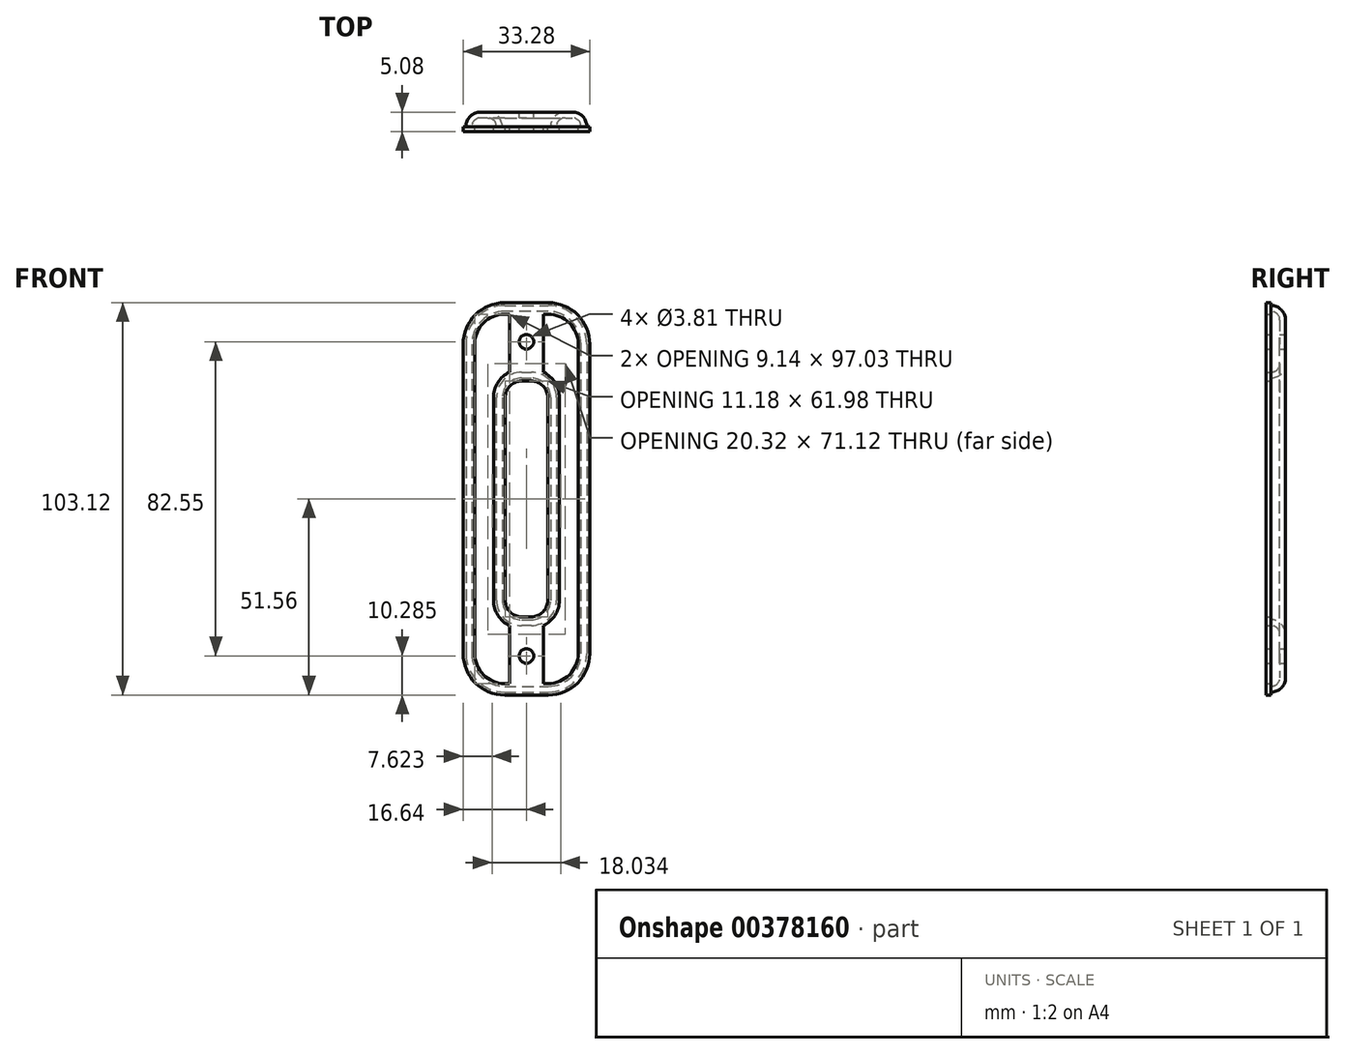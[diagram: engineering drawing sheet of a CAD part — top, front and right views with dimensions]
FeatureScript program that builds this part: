
annotation { "Feature Type Name" : "Feature", "Feature Type Description" : "" }
export const myFeature = defineFeature(function(context is Context, id is Id, definition is map)
    precondition{}
    {
        {
            var Q0;
            Q0=qCreatedBy(makeId("Front.planeOp"),FACE);
            var sketch = newSketch(context, id + "F0", { "sketchPlane" : qUnion([Q0])});
            skLineSegment(sketch, "E0.bottom", {"start": v(-6.35, 31.75) * mm, "end": v(6.35, 31.75) * mm});
            skLineSegment(sketch, "E0.top", {"start": v(-6.35, -31.75) * mm, "end": v(6.35, -31.75) * mm});
            skLineSegment(sketch, "E0.left", {"start": v(-6.35, 31.75) * mm, "end": v(-6.35, -31.75) * mm});
            skLineSegment(sketch, "E0.right", {"start": v(6.35, 31.75) * mm, "end": v(6.35, -31.75) * mm});
            skPoint(sketch, "E0.middle", {"position": v(0, 0) * mm});
            skLineSegment(sketch, "E1.bottom", {"start": v(-15.88, 50.8) * mm, "end": v(15.87, 50.8) * mm});
            skLineSegment(sketch, "E1.top", {"start": v(-15.87, -50.8) * mm, "end": v(15.88, -50.8) * mm});
            skLineSegment(sketch, "E1.left", {"start": v(-15.88, 50.8) * mm, "end": v(-15.87, -50.8) * mm});
            skLineSegment(sketch, "E1.right", {"start": v(15.87, 50.8) * mm, "end": v(15.88, -50.8) * mm});
            skSolve(sketch);
        }
        {
            var Q0;
            Q0 = qSketchRegion(id + "F0", true);
            extrude(context, id + "F1", {"entities" : qUnion([Q0]), "depth" : 3.8 * mm});
        }
        {
            var Q0;
            Q0=makeQuery(id+"F1.opExtrude","SWEPT_EDGE",EDGE,{"disambiguationData":[OSD([sQuery(id+"F0.wireOp",EDGE,"E1.bottom"),sQuery(id+"F0.wireOp",EDGE,"E1.left")])]});
            var Q1;
            Q1=makeQuery(id+"F1.opExtrude","SWEPT_EDGE",EDGE,{"disambiguationData":[OSD([sQuery(id+"F0.wireOp",EDGE,"E1.bottom"),sQuery(id+"F0.wireOp",EDGE,"E1.right")])]});
            var Q2;
            Q2=makeQuery(id+"F1.opExtrude","SWEPT_EDGE",EDGE,{"disambiguationData":[OSD([sQuery(id+"F0.wireOp",EDGE,"E1.top"),sQuery(id+"F0.wireOp",EDGE,"E1.right")])]});
            var Q3;
            Q3=makeQuery(id+"F1.opExtrude","SWEPT_EDGE",EDGE,{"disambiguationData":[OSD([sQuery(id+"F0.wireOp",EDGE,"E1.top"),sQuery(id+"F0.wireOp",EDGE,"E1.left")])]});
            fillet(context, id + "F2", {"entities" : qUnion([Q0, Q1, Q2, Q3]), "radius" : 10.16 * mm, "tangentPropagation" : true, "allowEdgeOverflow" : false});
        }
        {
            var Q0;
            Q0=makeQuery(id+"F1.opExtrude","SWEPT_EDGE",EDGE,{"disambiguationData":[OSD([sQuery(id+"F0.wireOp",EDGE,"E0.bottom"),sQuery(id+"F0.wireOp",EDGE,"E0.left")])]});
            var Q1;
            Q1=makeQuery(id+"F1.opExtrude","SWEPT_EDGE",EDGE,{"disambiguationData":[OSD([sQuery(id+"F0.wireOp",EDGE,"E0.bottom"),sQuery(id+"F0.wireOp",EDGE,"E0.right")])]});
            var Q2;
            Q2=makeQuery(id+"F1.opExtrude","SWEPT_EDGE",EDGE,{"disambiguationData":[OSD([sQuery(id+"F0.wireOp",EDGE,"E0.top"),sQuery(id+"F0.wireOp",EDGE,"E0.left")])]});
            var Q3;
            Q3=makeQuery(id+"F1.opExtrude","SWEPT_EDGE",EDGE,{"disambiguationData":[OSD([sQuery(id+"F0.wireOp",EDGE,"E0.top"),sQuery(id+"F0.wireOp",EDGE,"E0.right")])]});
            fillet(context, id + "F3", {"entities" : qUnion([Q0, Q1, Q2, Q3]), "radius" : 5.08 * mm, "tangentPropagation" : true, "allowEdgeOverflow" : false});
        }
        {
            var Q0;
            Q0=makeQuery(id+"F1.opExtrude","CAP_EDGE",EDGE,{"disambiguationData":[OSD([sQuery(id+"F0.wireOp",EDGE,"E1.right")])],"isStart":true});
            var Q1;
            {var subQ0=sQuery(id+"F0.wireOp",EDGE,"E0.right");var subQ1=sQuery(id+"F0.wireOp",EDGE,"E0.bottom");Q1=makeQuery(id+"F3.opFillet","BLEND_EDGE",EDGE,{"blendedFrom":[makeQuery(id+"F1.opExtrude","SWEPT_EDGE",EDGE,{"disambiguationData":[OSD([subQ1,subQ0])]}),makeQuery(id+"F1.opExtrude","CAP_FACE",FACE,{"disambiguationData":[OSD([subQ1,sQuery(id+"F0.wireOp",EDGE,"E0.top"),sQuery(id+"F0.wireOp",EDGE,"E0.left"),subQ0,sQuery(id+"F0.wireOp",EDGE,"E1.bottom"),sQuery(id+"F0.wireOp",EDGE,"E1.top"),sQuery(id+"F0.wireOp",EDGE,"E1.left"),sQuery(id+"F0.wireOp",EDGE,"E1.right")])],"isStart":true})],"blendedInto":[makeQuery(id+"F1.opExtrude","CAP_FACE",FACE,{"disambiguationData":[OSD([subQ1,sQuery(id+"F0.wireOp",EDGE,"E0.top"),sQuery(id+"F0.wireOp",EDGE,"E0.left"),subQ0,sQuery(id+"F0.wireOp",EDGE,"E1.bottom"),sQuery(id+"F0.wireOp",EDGE,"E1.top"),sQuery(id+"F0.wireOp",EDGE,"E1.left"),sQuery(id+"F0.wireOp",EDGE,"E1.right")])],"isStart":true})]});}
            fillet(context, id + "F4", {"entities" : qUnion([Q0, Q1]), "radius" : 3.8 * mm, "tangentPropagation" : true, "allowEdgeOverflow" : false});
        }
        {
            var Q0;
            Q0=makeQuery(id+"F1.opExtrude","CAP_FACE",FACE,{"disambiguationData":[OSD([sQuery(id+"F0.wireOp",EDGE,"E0.bottom"),sQuery(id+"F0.wireOp",EDGE,"E0.top"),sQuery(id+"F0.wireOp",EDGE,"E0.left"),sQuery(id+"F0.wireOp",EDGE,"E0.right"),sQuery(id+"F0.wireOp",EDGE,"E1.bottom"),sQuery(id+"F0.wireOp",EDGE,"E1.top"),sQuery(id+"F0.wireOp",EDGE,"E1.left"),sQuery(id+"F0.wireOp",EDGE,"E1.right")])],"isStart":false});
            shell(context, id + "F5", {"entities" : qUnion([Q0]), "thickness" : 1.52 * mm});
        }
        {
            var Q0;
            Q0=makeQuery(id+"F1.opExtrude","CAP_FACE",FACE,{"disambiguationData":[OSD([sQuery(id+"F0.wireOp",EDGE,"E0.bottom"),sQuery(id+"F0.wireOp",EDGE,"E0.top"),sQuery(id+"F0.wireOp",EDGE,"E0.left"),sQuery(id+"F0.wireOp",EDGE,"E0.right"),sQuery(id+"F0.wireOp",EDGE,"E1.bottom"),sQuery(id+"F0.wireOp",EDGE,"E1.top"),sQuery(id+"F0.wireOp",EDGE,"E1.left"),sQuery(id+"F0.wireOp",EDGE,"E1.right")])],"isStart":true});
            var sketch = newSketch(context, id + "F6", { "sketchPlane" : qUnion([Q0])});
            skCircle(sketch, "E2", {"center": v(0, 41.28) * mm, "radius": 1.9 * mm});
            skCircle(sketch, "E3", {"center": v(0, -41.28) * mm, "radius": 1.9 * mm});
            skLineSegment(sketch, "E4", {"start": v(0, 41.28) * mm, "end": v(0, -41.28) * mm, "construction": true});
            skPoint(sketch, "E5", {"position": v(0, 0) * mm});
            skSolve(sketch);
        }
        {
            var Q0;
            Q0 = qSketchRegion(id + "F6", true);
            var Q1;
            {var subQ0=sQuery(id+"F0.wireOp",EDGE,"E1.right");var subQ1=sQuery(id+"F0.wireOp",EDGE,"E1.left");var subQ2=sQuery(id+"F0.wireOp",EDGE,"E1.top");var subQ3=sQuery(id+"F0.wireOp",EDGE,"E1.bottom");var subQ4=sQuery(id+"F0.wireOp",EDGE,"E0.right");var subQ5=sQuery(id+"F0.wireOp",EDGE,"E0.left");var subQ6=sQuery(id+"F0.wireOp",EDGE,"E0.top");var subQ7=sQuery(id+"F0.wireOp",EDGE,"E0.bottom");Q1=makeQuery(id+"F5.opShell","OFFSET_FACE",FACE,{"disambiguationData":[OSD([subQ7,subQ6,subQ5,subQ4,subQ3,subQ2,subQ1,subQ0]),TDD([makeQuery(id+"F1.opExtrude","CAP_FACE",FACE,{"disambiguationData":[OSD([subQ7,subQ6,subQ5,subQ4,subQ3,subQ2,subQ1,subQ0])],"isStart":true})])]});}
            extrude(context, id + "F7", {"entities" : qUnion([Q0]), "operationType" : NewBodyOperationType.REMOVE, "endBound" : BoundingType.UP_TO_SURFACE, "oppositeDirection" : true, "endBoundEntityFace" : qUnion([Q1]), "depth" : 25.4 * mm});
        }
        {
            var Q0;
            Q0=makeQuery(id+"F1.opExtrude","CAP_FACE",FACE,{"disambiguationData":[OSD([sQuery(id+"F0.wireOp",EDGE,"E0.bottom"),sQuery(id+"F0.wireOp",EDGE,"E0.top"),sQuery(id+"F0.wireOp",EDGE,"E0.left"),sQuery(id+"F0.wireOp",EDGE,"E0.right"),sQuery(id+"F0.wireOp",EDGE,"E1.bottom"),sQuery(id+"F0.wireOp",EDGE,"E1.top"),sQuery(id+"F0.wireOp",EDGE,"E1.left"),sQuery(id+"F0.wireOp",EDGE,"E1.right")])],"isStart":false});
            var sketch = newSketch(context, id + "F8", { "sketchPlane" : qUnion([Q0])});
            skLineSegment(sketch, "E6", {"start": v(-16.64, 40.64) * mm, "end": v(-16.64, -40.64) * mm});
            skLineSegment(sketch, "E7", {"start": v(-5.71, -51.56) * mm, "end": v(5.72, -51.56) * mm});
            skLineSegment(sketch, "E8", {"start": v(16.64, -40.64) * mm, "end": v(16.64, 40.64) * mm});
            skLineSegment(sketch, "E9", {"start": v(5.72, 51.56) * mm, "end": v(-5.71, 51.56) * mm});
            skArc(sketch, "E10", {"start": v(-5.71, 51.56) * mm, "mid": v(-13.44, 48.36) * mm, "end": v(-16.64, 40.64) * mm});
            skArc(sketch, "E11", {"start": v(16.64, 40.64) * mm, "mid": v(13.44, 48.36) * mm, "end": v(5.72, 51.56) * mm});
            skArc(sketch, "E12", {"start": v(-16.64, -40.64) * mm, "mid": v(-13.44, -48.36) * mm, "end": v(-5.71, -51.56) * mm});
            skArc(sketch, "E13", {"start": v(5.72, -51.56) * mm, "mid": v(13.44, -48.36) * mm, "end": v(16.64, -40.64) * mm});
            skLineSegment(sketch, "E14", {"start": v(-5.59, 26.67) * mm, "end": v(-5.59, -26.67) * mm});
            skLineSegment(sketch, "E15", {"start": v(-1.27, 30.99) * mm, "end": v(1.27, 30.99) * mm});
            skLineSegment(sketch, "E16", {"start": v(-1.27, -30.99) * mm, "end": v(1.27, -30.99) * mm});
            skLineSegment(sketch, "E17", {"start": v(5.59, 26.67) * mm, "end": v(5.59, -26.67) * mm});
            skLineSegment(sketch, "E18", {"start": v(5.59, 26.67) * mm, "end": v(6.35, 26.67) * mm, "construction": true});
            skLineSegment(sketch, "E19", {"start": v(15.87, 40.64) * mm, "end": v(16.64, 40.64) * mm, "construction": true});
            skArc(sketch, "E20", {"start": v(-1.27, 30.99) * mm, "mid": v(-4.32, 29.72) * mm, "end": v(-5.59, 26.67) * mm});
            skArc(sketch, "E21", {"start": v(5.59, 26.67) * mm, "mid": v(4.32, 29.72) * mm, "end": v(1.27, 30.99) * mm});
            skArc(sketch, "E22", {"start": v(-5.59, -26.67) * mm, "mid": v(-4.32, -29.72) * mm, "end": v(-1.27, -30.99) * mm});
            skArc(sketch, "E23", {"start": v(1.27, -30.99) * mm, "mid": v(4.32, -29.72) * mm, "end": v(5.59, -26.67) * mm});
            skCircle(sketch, "E24", {"center": v(0, 41.28) * mm, "radius": 1.9 * mm});
            skCircle(sketch, "E25", {"center": v(0, -41.28) * mm, "radius": 1.9 * mm});
            skLineSegment(sketch, "E26", {"start": v(-4.44, 48.51) * mm, "end": v(-4.44, 33.32) * mm});
            skLineSegment(sketch, "E27", {"start": v(4.45, 48.51) * mm, "end": v(4.45, 33.32) * mm});
            skLineSegment(sketch, "E28", {"start": v(-8.64, 26.67) * mm, "end": v(-8.64, -26.67) * mm});
            skLineSegment(sketch, "E29", {"start": v(8.64, 26.67) * mm, "end": v(8.64, -26.67) * mm});
            skLineSegment(sketch, "E30", {"start": v(-13.59, 40.64) * mm, "end": v(-13.59, -40.64) * mm});
            skLineSegment(sketch, "E31", {"start": v(13.59, 40.64) * mm, "end": v(13.59, -40.64) * mm});
            skLineSegment(sketch, "E32", {"start": v(-4.45, 48.51) * mm, "end": v(-5.71, 48.51) * mm});
            skLineSegment(sketch, "E33", {"start": v(4.45, 48.51) * mm, "end": v(5.71, 48.51) * mm});
            skLineSegment(sketch, "E34", {"start": v(-5.72, -48.51) * mm, "end": v(-4.44, -48.51) * mm});
            skLineSegment(sketch, "E35", {"start": v(-4.44, -48.51) * mm, "end": v(-4.44, -33.32) * mm});
            skLineSegment(sketch, "E36", {"start": v(5.71, -48.51) * mm, "end": v(4.45, -48.51) * mm});
            skLineSegment(sketch, "E37", {"start": v(4.45, -48.51) * mm, "end": v(4.45, -33.32) * mm});
            skArc(sketch, "E38", {"start": v(-13.59, -40.64) * mm, "mid": v(-11.28, -46.2) * mm, "end": v(-5.72, -48.51) * mm});
            skArc(sketch, "E39", {"start": v(5.71, -48.51) * mm, "mid": v(11.28, -46.2) * mm, "end": v(13.59, -40.64) * mm});
            skArc(sketch, "E40", {"start": v(4.45, -33.32) * mm, "mid": v(7.5, -30.6) * mm, "end": v(8.64, -26.67) * mm});
            skArc(sketch, "E41", {"start": v(-8.64, -26.67) * mm, "mid": v(-7.5, -30.6) * mm, "end": v(-4.44, -33.32) * mm});
            skArc(sketch, "E42", {"start": v(-4.44, 33.32) * mm, "mid": v(-7.5, 30.6) * mm, "end": v(-8.64, 26.67) * mm});
            skArc(sketch, "E43", {"start": v(8.64, 26.67) * mm, "mid": v(7.5, 30.6) * mm, "end": v(4.45, 33.32) * mm});
            skArc(sketch, "E44", {"start": v(13.59, 40.64) * mm, "mid": v(11.28, 46.2) * mm, "end": v(5.71, 48.51) * mm});
            skArc(sketch, "E45", {"start": v(-5.71, 48.51) * mm, "mid": v(-11.28, 46.2) * mm, "end": v(-13.59, 40.64) * mm});
            skLineSegment(sketch, "E46", {"start": v(-4.45, 48.51) * mm, "end": v(4.45, 48.51) * mm, "construction": true});
            skPoint(sketch, "E47", {"position": v(0, 48.51) * mm});
            skLineSegment(sketch, "E48", {"start": v(-4.44, -48.51) * mm, "end": v(4.45, -48.51) * mm, "construction": true});
            skLineSegment(sketch, "E49", {"start": v(5.72, 48.51) * mm, "end": v(5.72, 49.28) * mm, "construction": true});
            skLineSegment(sketch, "E50", {"start": v(8.64, 26.67) * mm, "end": v(7.87, 26.67) * mm, "construction": true});
            skSolve(sketch);
        }
        {
            var Q0;
            Q0 = qSketchRegion(id + "F8", true);
            extrude(context, id + "F9", {"entities" : qUnion([Q0]), "depth" : 1.27 * mm});
        }
    });
